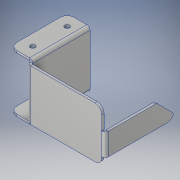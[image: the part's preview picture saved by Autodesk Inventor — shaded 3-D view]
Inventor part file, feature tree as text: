
AUTODESK INVENTOR PART (.ipt)
format: ipt  version: 2019 (Build 230136000, 136)  size: 259,072 bytes
history: native  units: mm
features: sheet_metal_op x9, other x5, sketch x4, chamfer x2, hole x1
ambient origin geometry x8: Origin, YZ Plane, XZ Plane, XY Plane, X Axis, Y Axis, Z Axis, Center Point
bodies: Solid1 (feature_tree)
feature tree (21):
  sheet_metal_op  "Contour Flange1"
  sheet_metal_op  "Flange2"
  sheet_metal_op  "Flange3"
  hole  "Hole1"  [1 undecoded]
  other  "Corner Chamfer1"
  chamfer  "Corner Round2"
  chamfer  "Corner Round3"
  sketch  "Sketch1"  dims[d0=50.0mm d1=20.0mm]
  other  "Plate1"
  sheet_metal_op  "Bend1"
  sheet_metal_op  "Corner1"
  sketch  "Sketch3"  dims[d2=2.0mm]
  other  "Plate3"
  sheet_metal_op  "Bend3"
  sheet_metal_op  "Corner3"
  sketch  "Sketch4"  dims[d3=0.2mm d4=0.2mm d5=0.2mm d6=0.8mm]
  other  "Plate4"
  sheet_metal_op  "Bend4"
  sheet_metal_op  "Corner4"
  sketch  "Sketch5"  dims[d7=50.0mm d8=0.8mm d9=2.0mm d10=8.0mm d11=0.2mm d12=0.8mm d23=0.2mm d24=0.2mm d25=0.2mm d26=0.8mm d27=65.0mm d28=90.0deg d29=0.8mm d30=8.0mm d31=0.2mm d32=0.8mm d33=0.2mm d34=0.2mm d35=0.2mm d36=0.8mm d37=18.4mm d38=6.6mm d39=60.0mm d40=90.0deg d41=0.8mm d42=8.0mm d43=0.2mm d44=0.8mm d45=10.0mm d46=10.0mm d47=4.2mm d48=4.2mm d49=6.0mm d50=4.0mm d51=2.0mm d52=90.0deg d53=2.0mm d54=20.594885mm d57=15.0mm d58=6.0mm d59=45.0deg d60=6.0mm d61=2.0mm d62=6.0mm]
  other  "Definition1"
note: 1 required parameter value undecoded (feature->parameter linkage not recoverable at this tier; creation-order binding heuristic only, values carry confidence <= 0.55)
